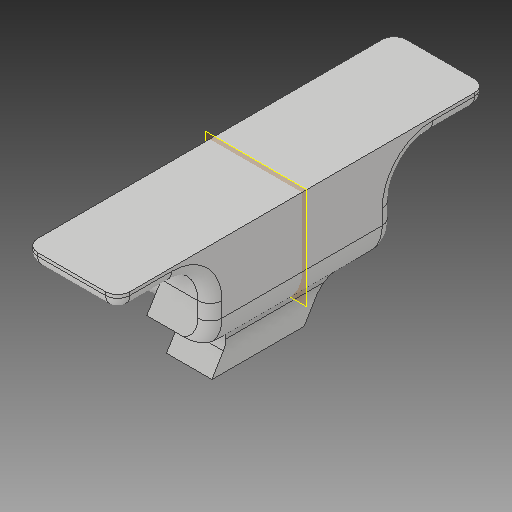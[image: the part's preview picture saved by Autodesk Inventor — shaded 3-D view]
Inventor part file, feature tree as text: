
AUTODESK INVENTOR PART (.ipt)
format: ipt  version: 2018 (Build 220112000, 112)  size: 200,704 bytes
history: native  units: in
note: dims shown in document units (in); Inventor stores cm internally (conversion verified against a paired STEP export)
features: sketch x9, other x3, plane x3
ambient origin geometry x8: Origin, YZ Plane, XZ Plane, XY Plane, X Axis, Y Axis, Z Axis, Center Point
bodies: Solid1 (feature_tree)
feature tree (15):
  other  "bottomARM.ipt"
  other  "Solid1::bottomARM.ipt"
  other  "TaggingFeature1"
  sketch  "Sketch1"  dims[d0=0.3937in]
  sketch  "Sketch3"
  sketch  "Sketch4"
  sketch  "Sketch6"
  sketch  "Sketch7"
  sketch  "Sketch8"
  sketch  "Sketch10"
  sketch  "Sketch11"
  sketch  "Sketch12"
  plane  "Work Plane1"
  plane  "Work Plane2"
  plane  "Work Plane3"
